# Revit family: Flat roof window FAKRO DMF DU8
name_source: partatom
category: Okna
revit_build: Autodesk Revit 2015 (Build: 20140606_1530(x64)
units: mm (PartAtom-declared; Revit-internal decimal feet)

## types (9) — shared parameters
Apron Material = Fakro - aluminium RAL7022
Bimobject Category = Windows - Roof Windows
CSI MasterFormat 2016 Code = 08 60 00
CSI MasterFormat 2016 Title = Roof Windows and Skylights
CSI UniFormat II Code = B3020
CSI UniFormat II Title = Roof Openings
Glazing = Fakro - Glass
IFC Classification = Window
Kod zespołu = B3020110
Material External = Fakro - aluminium RAL7022
Material Internal = Fakro - frame - PVC RAL 9010
Model = DMF DU8
NBS Reference = 59-72
NBS Reference Description = Roof Window Units
Opis = Flat roof window
Producent = FAKRO
UNSPC Category = Skylights
UNSPC Code = 301718
URL = www.fakro.com
Uniclass 1.4 Code = JL1
Uniclass 1.4 Description = Windows/Rooflights/Screens/Louvres
Uniclass 2.0 Code = PR-59-72
Uniclass 2.0 Description = Roof Window Units
Uniclass 2015 Code = PR_30_59_72_77
Uniclass 2015 Title = Skylights
Uw [W/m2K] EN 14351-1:2006+A1:2010 for window dimension 1.23x1.48m = 0.64
Wysokość = 190 mm
air permeability class EN 14351-1:2006+A1:2010 = 4
colour = white RAL 9010
glass structure = 6H-10-4HT-10-4HT-12-44.2T
glazing U-value [W/m2K] EN 14351-1:2006+A1:2010 = 0.4
impact resistance class EN 14351-1:2006+A1:2010 = 5
light transmittance factor tv EN 14351-1:2006+A1:2010 = 0.49
material = multi-chamber PVC profiles
opening method = top hung
operation mode = manual
reaction to fire EN 14351-1:2006+A1:2010 = B-s2, d0
resistance to snow load EN 14351-1:2006+A1:2010 = 6H-10-4H-10-4H-12-44.2
roof angle = 2 -15
solar factor [ g] EN 14351-1:2006+A1:2010 = 0.38
watertightness / unshielded (A) EN 14351-1:2006+A1:2010 = E1200
window acoustic performance Rw [dB] EN 14351-1:2006+A1:2010 = 33(-1;-3)

## per-type parameters (varying)
| type | Length | Length with base | Obj Type | Szerokość | Width with base | glazing area | resistance to wind load EN 14351-1:2006+A1:2010 | window internal area | window perimeter | window weight |
| DMF DU8 - 01K - 60x60 | 600 mm  [stored 1.9685 ft] | 820 mm | 1 mm  [stored 0.00328084 ft] | 600 mm  [stored 1.9685 ft] | 820 mm | 0.23 m² | C5/B5 | 0.27 m² | 3280 mm | 44.00 kg |
| DMF DU8 - 02K - 60x90 | 900 mm  [stored 2.95276 ft] | 1120 mm | 2 mm  [stored 0.00656168 ft] | 600 mm  [stored 1.9685 ft] | 820 mm | 0.37 m² | C5/B5 | 0.42 m² | 3880 mm | 59.00 kg |
| DMF DU8 - 03K - 70x70 | 700 mm  [stored 2.29659 ft] | 920 mm | 3 mm  [stored 0.00984252 ft] | 700 mm  [stored 2.29659 ft] | 920 mm | 0.33 m² | C5/B5 | 0.38 m² | 3680 mm | 55.00 kg |
| DMF DU8 - 04K - 80x80 | 800 mm  [stored 2.62467 ft] | 1020 mm | 4 mm  [stored 0.0131234 ft] | 800 mm  [stored 2.62467 ft] | 1020 mm | 0.46 m² | C5/B5 | 0.51 m² | 4080 mm | 66.00 kg |
| DMF DU8 - 05K - 90x90 | 900 mm  [stored 2.95276 ft] | 1120 mm | 5 mm  [stored 0.0164042 ft] | 900 mm  [stored 2.95276 ft] | 1120 mm | 0.6 m² | C5/B5 | 0.67 m² | 4480 mm | 79.00 kg |
| DMF DU8 - 06K - 90x120 | 1200 mm | 1420 mm | 6 mm  [stored 0.019685 ft] | 900 mm  [stored 2.95276 ft] | 1120 mm | 0.83 m² | C5/B5 | 0.91 m² | 5080 mm | 98.00 kg |
| DMF DU8 - 07K - 100x100 | 1000 mm  [stored 3.28084 ft] | 1220 mm  [stored 4.00262 ft] | 7 mm  [stored 0.0229659 ft] | 1000 mm  [stored 3.28084 ft] | 1220 mm  [stored 4.00262 ft] | 0.77 m² | C5/B5 | 0.84 m² | 4880 mm  [stored 16.0105 ft] | 92.00 kg |
| DMF DU8 - 10K - 100x150 | 1500 mm  [stored 4.92126 ft] | 1720 mm | 10 mm  [stored 0.0328084 ft] | 1000 mm  [stored 3.28084 ft] | 1220 mm  [stored 4.00262 ft] | 1.21 m² | C2/B2 | 1.3 m² | 5880 mm | 128.00 kg |
| DMF DU8 - 08K - 120x120 | 1200 mm | 1420 mm | 8 mm  [stored 0.0262467 ft] | 1200 mm | 1420 mm | 1.16 m² | C5/B5 | 1.25 m² | 5680 mm | 123.00 kg |

note: [stored X ft] marks values corroborated as IEEE doubles in the binary element streams (Revit-internal decimal feet)
